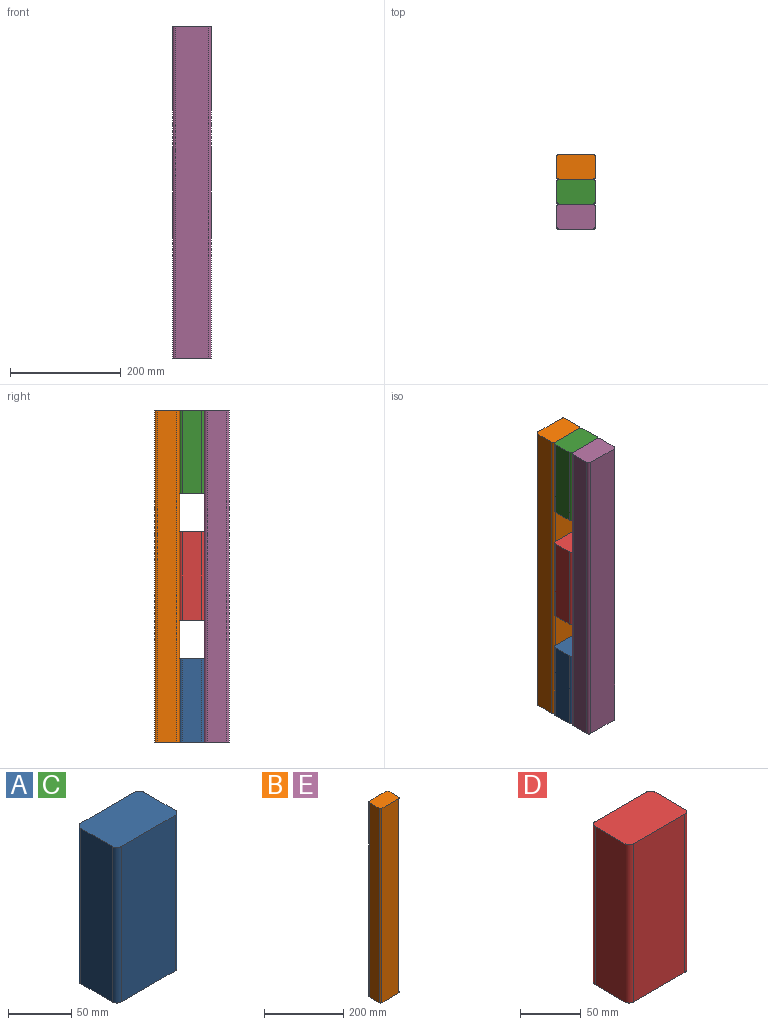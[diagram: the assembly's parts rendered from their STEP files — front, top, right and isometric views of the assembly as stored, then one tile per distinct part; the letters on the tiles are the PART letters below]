
ASSEMBLY  parts=5 mates=4
PART A: 10 faces, bbox 70x45x150 mm
  f0: plane 150x60mm, normal (0,1,0), area 9000mm2, adj f4,f5,f6,f9
  f1: plane 150x35mm, normal (-1,0,0), area 5250mm2, adj f4,f5,f6,f7
  f2: plane 150x60mm, normal (0,-1,0), area 9000mm2, adj f4,f5,f7,f8
  f3: plane 150x35mm, normal (1,0,0), area 5250mm2, adj f4,f5,f8,f9
  f4: plane 70x45mm, normal (0,0,1), area 3128.5mm2, adj f0,f1,f2,f3,f6,f7,f8,f9
  f5: plane 70x45mm, normal (0,0,-1), area 3128.5mm2, adj f0,f1,f2,f3,f6,f7,f8,f9
  f6: cylinder r=5mm len=150mm, axis (0,0,1), area 1178.1mm2, adj f0,f1,f4,f5
  f7: cylinder r=5mm len=150mm, axis (0,0,-1), area 1178.1mm2, adj f1,f2,f4,f5
  f8: cylinder r=5mm len=150mm, axis (0,0,1), area 1178.1mm2, adj f2,f3,f4,f5
  f9: cylinder r=5mm len=150mm, axis (0,0,-1), area 1178.1mm2, adj f0,f3,f4,f5
PART B: 10 faces, bbox 70x45x600 mm
  f0: plane 600x60mm, normal (0,1,0), area 36000mm2, adj f4,f5,f6,f9
  f1: plane 600x35mm, normal (-1,0,0), area 21000mm2, adj f4,f5,f6,f7
  f2: plane 600x60mm, normal (0,-1,0), area 36000mm2, adj f4,f5,f7,f8
  f3: plane 600x35mm, normal (1,0,0), area 21000mm2, adj f4,f5,f8,f9
  f4: plane 70x45mm, normal (0,0,1), area 3128.5mm2, adj f0,f1,f2,f3,f6,f7,f8,f9
  f5: plane 70x45mm, normal (0,0,-1), area 3128.5mm2, adj f0,f1,f2,f3,f6,f7,f8,f9
  f6: cylinder r=5mm len=600mm, axis (0,0,1), area 4712.4mm2, adj f0,f1,f4,f5
  f7: cylinder r=5mm len=600mm, axis (0,0,-1), area 4712.4mm2, adj f1,f2,f4,f5
  f8: cylinder r=5mm len=600mm, axis (0,0,1), area 4712.4mm2, adj f2,f3,f4,f5
  f9: cylinder r=5mm len=600mm, axis (0,0,-1), area 4712.4mm2, adj f0,f3,f4,f5
PART C: same geometry as A
PART D: 10 faces, bbox 70x45x160 mm
  f0: plane 160x60mm, normal (0,1,0), area 9600mm2, adj f4,f5,f6,f9
  f1: plane 160x35mm, normal (-1,0,0), area 5600mm2, adj f4,f5,f6,f7
  f2: plane 160x60mm, normal (0,-1,0), area 9600mm2, adj f4,f5,f7,f8
  f3: plane 160x35mm, normal (1,0,0), area 5600mm2, adj f4,f5,f8,f9
  f4: plane 70x45mm, normal (0,0,1), area 3128.5mm2, adj f0,f1,f2,f3,f6,f7,f8,f9
  f5: plane 70x45mm, normal (0,0,-1), area 3128.5mm2, adj f0,f1,f2,f3,f6,f7,f8,f9
  f6: cylinder r=5mm len=160mm, axis (0,0,1), area 1256.6mm2, adj f0,f1,f4,f5
  f7: cylinder r=5mm len=160mm, axis (0,0,-1), area 1256.6mm2, adj f1,f2,f4,f5
  f8: cylinder r=5mm len=160mm, axis (0,0,1), area 1256.6mm2, adj f2,f3,f4,f5
  f9: cylinder r=5mm len=160mm, axis (0,0,-1), area 1256.6mm2, adj f0,f3,f4,f5
PART E: same geometry as B
PLACE A t=(-611.87,-69.73,-255.27)mm
PLACE B t=(-611.87,-24.73,-255.27)mm
PLACE C t=(-611.87,-69.73,194.73)mm
PLACE D t=(-611.87,-69.73,-35.27)mm
PLACE E t=(-611.87,-114.73,-255.27)mm fixed
MATE fastened A.f2 <-> E.f0  axis (0,-1,0) through (-619.55,-98.51,-255.27)mm
MATE fastened E.f0 <-> C.f2  axis (0,1,0) through (-619.55,-98.51,344.73)mm
MATE fastened A.f0 <-> B.f2  axis (0,1,0) through (-619.55,-53.51,-255.27)mm
MATE fastened C.f0 <-> D.f0  axis (0,1,0) through (-619.55,-53.51,194.73)mm
